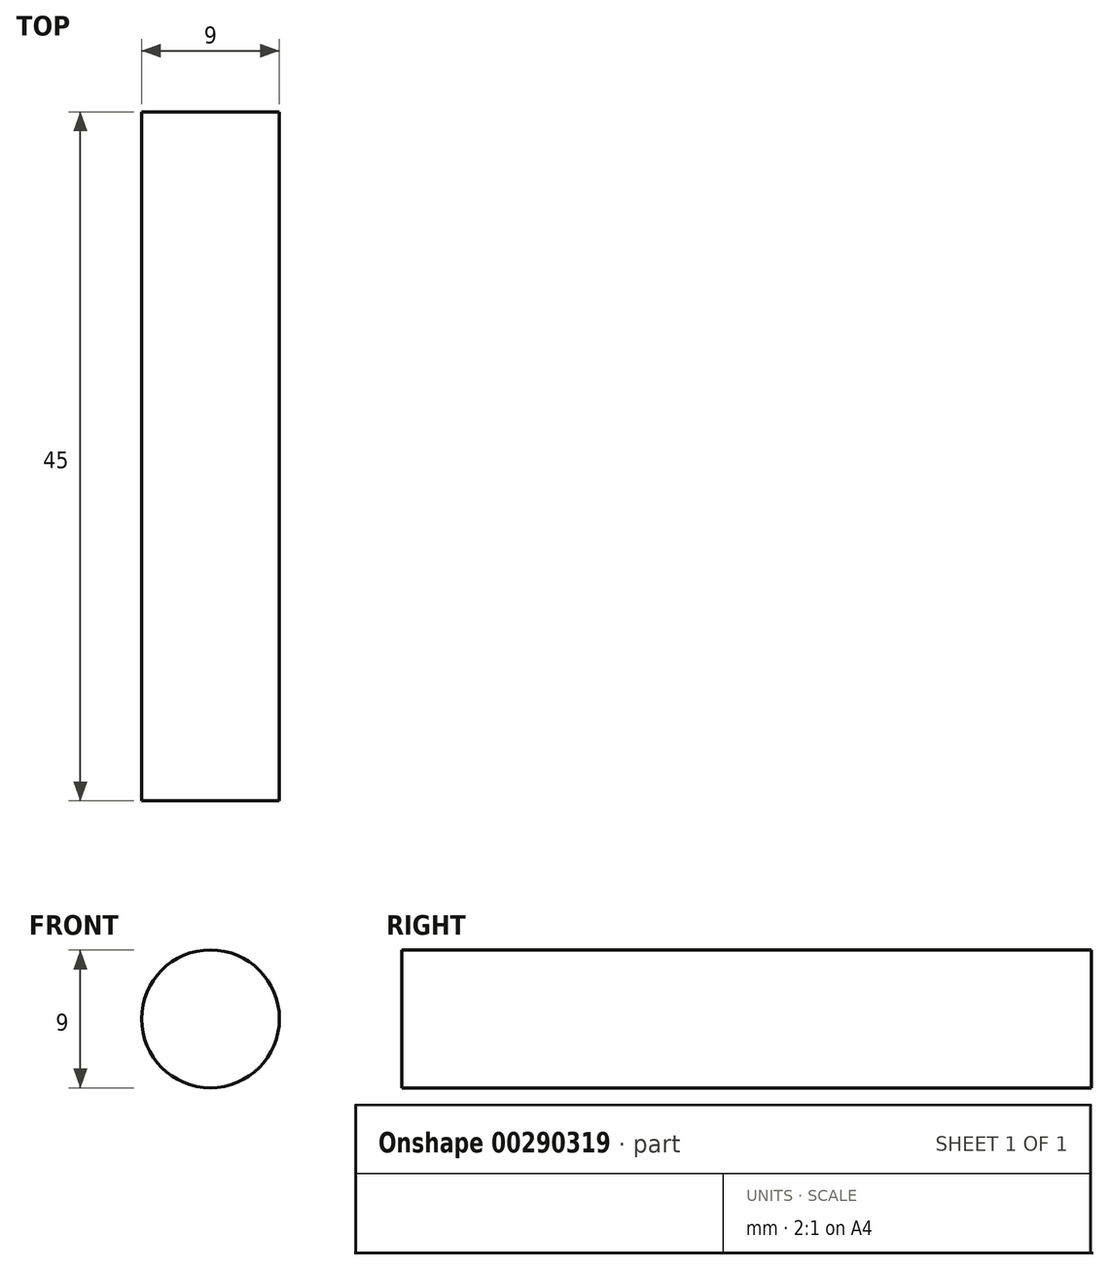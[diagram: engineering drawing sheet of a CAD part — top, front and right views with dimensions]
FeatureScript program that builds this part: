
annotation { "Feature Type Name" : "Feature", "Feature Type Description" : "" }
export const myFeature = defineFeature(function(context is Context, id is Id, definition is map)
    precondition{}
    {
        {
            var Q0;
            Q0=qCreatedBy(makeId("Front.planeOp"),FACE);
            var sketch = newSketch(context, id + "F0", { "sketchPlane" : qUnion([Q0])});
            skCircle(sketch, "E0", {"center": v(-0.43, 0.24) * mm, "radius": 4.5 * mm});
            skSolve(sketch);
        }
        {
            var Q0;
            Q0 = qSketchRegion(id + "F0", true);
            extrude(context, id + "F1", {"entities" : qUnion([Q0]), "endBound" : BoundingType.SYMMETRIC, "depth" : 45 * mm});
        }
    });
